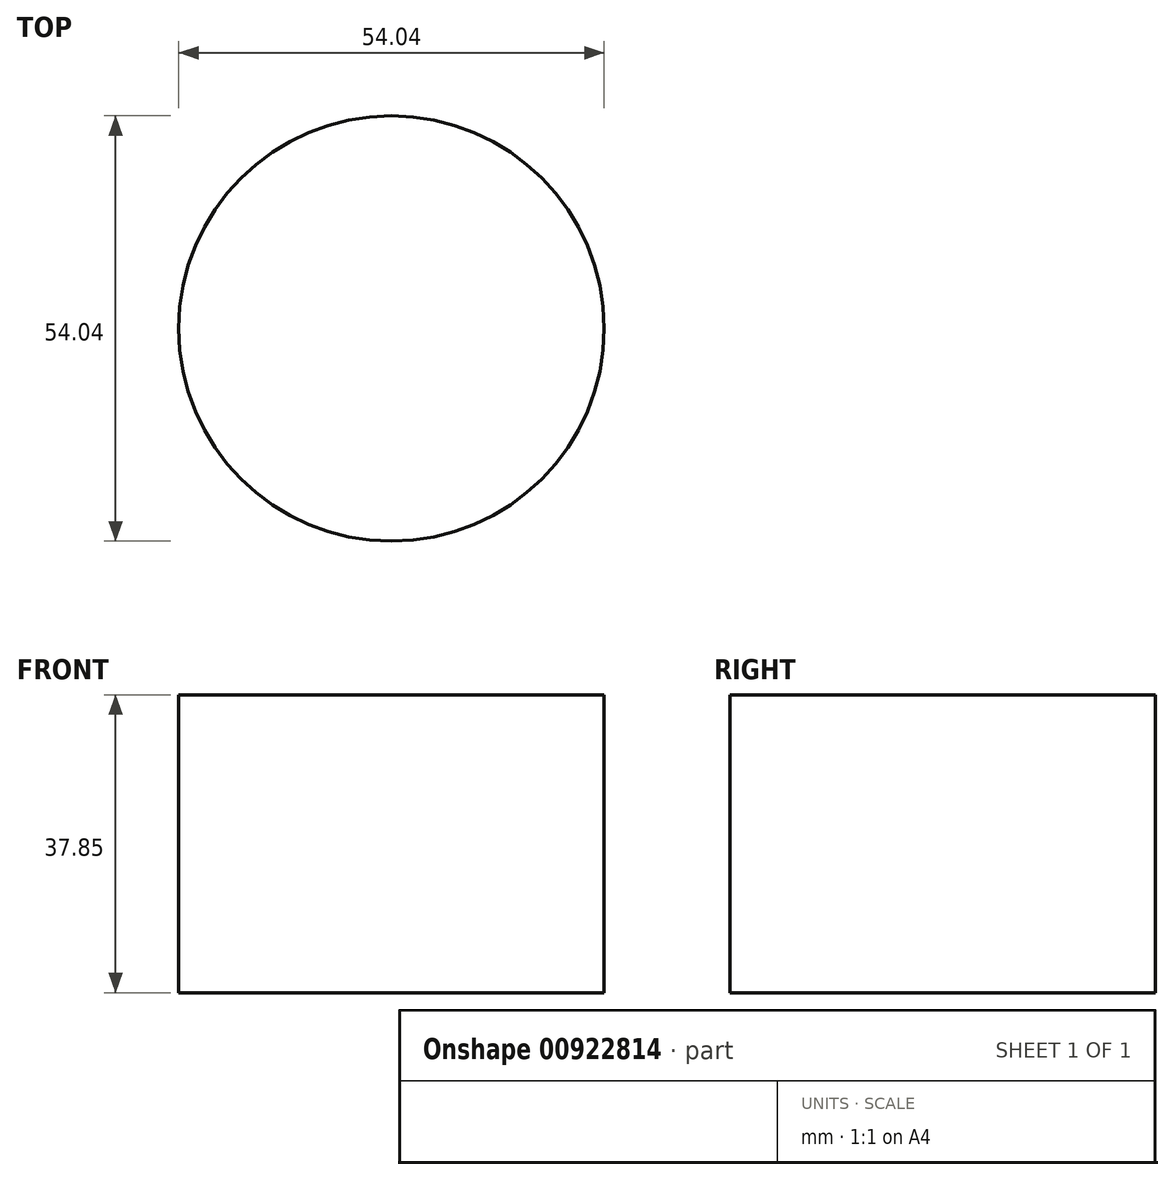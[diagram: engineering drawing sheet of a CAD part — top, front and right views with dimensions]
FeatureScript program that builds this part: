
annotation { "Feature Type Name" : "Feature", "Feature Type Description" : "" }
export const myFeature = defineFeature(function(context is Context, id is Id, definition is map)
    precondition{}
    {
        {
            var Q0;
            Q0=qCreatedBy(makeId("Top.planeOp"),FACE);
            var sketch = newSketch(context, id + "F0", { "sketchPlane" : qUnion([Q0])});
            skCircle(sketch, "E0", {"center": v(0, 0.45) * mm, "radius": 27.02 * mm});
            skSolve(sketch);
        }
        {
            var Q0;
            Q0 = qSketchRegion(id + "F0", true);
            extrude(context, id + "F1", {"entities" : qUnion([Q0]), "depth" : 37.85 * mm, "offsetDistance" : 25.4 * mm});
        }
    });
